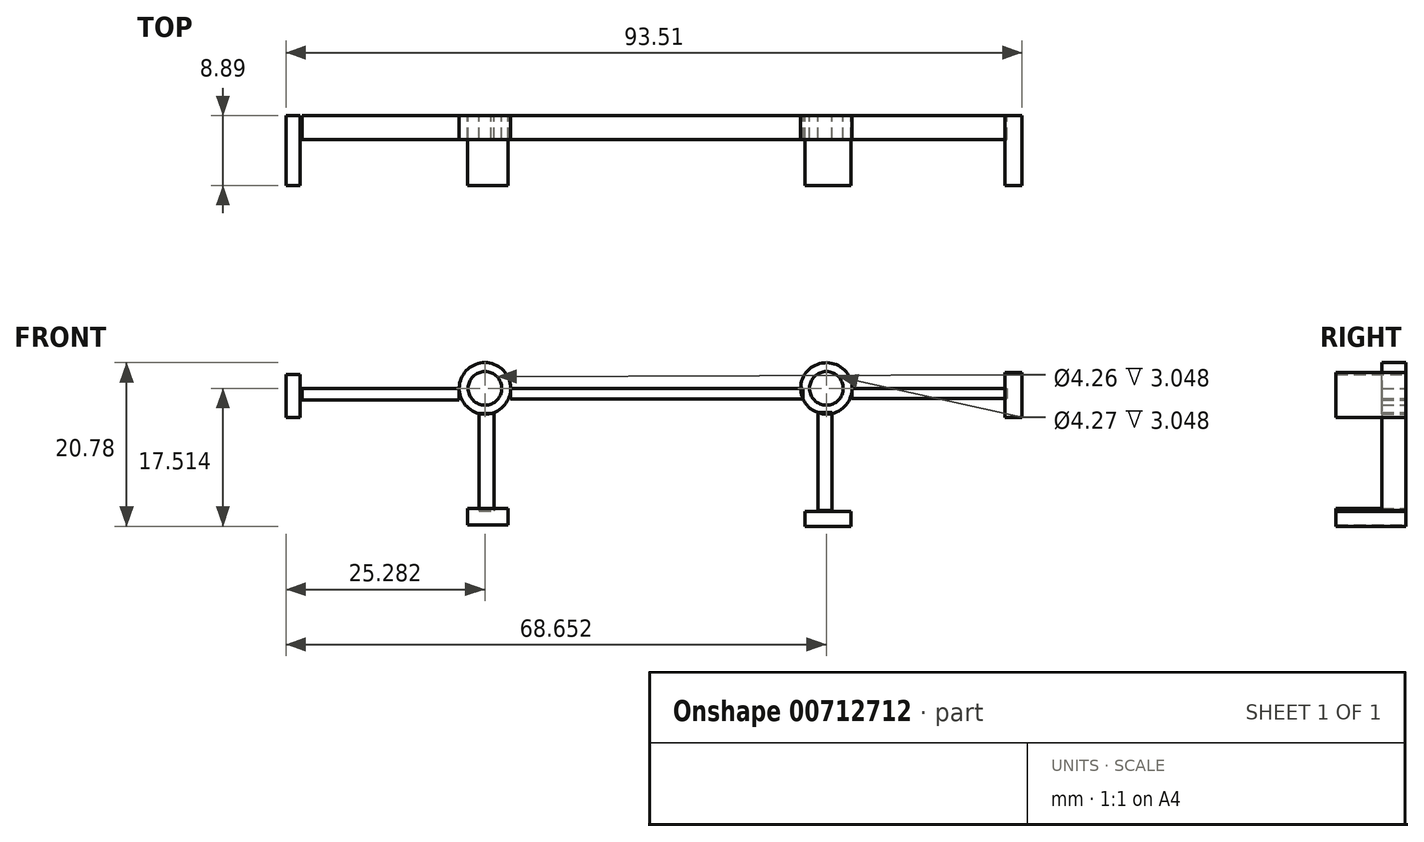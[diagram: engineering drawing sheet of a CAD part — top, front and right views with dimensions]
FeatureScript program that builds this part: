
annotation { "Feature Type Name" : "Feature", "Feature Type Description" : "" }
export const myFeature = defineFeature(function(context is Context, id is Id, definition is map)
    precondition{}
    {
        {
            var Q0;
            Q0=qCreatedBy(makeId("Front.planeOp"),FACE);
            var sketch = newSketch(context, id + "F0", { "sketchPlane" : qUnion([Q0])});
            skCircle(sketch, "E0", {"center": v(-24.54, 12.82) * mm, "radius": 3.27 * mm});
            skCircle(sketch, "E1", {"center": v(-24.54, 12.82) * mm, "radius": 2.13 * mm});
            skCircle(sketch, "E2", {"center": v(18.83, 12.82) * mm, "radius": 2.13 * mm});
            skCircle(sketch, "E3", {"center": v(18.83, 12.82) * mm, "radius": 3.26 * mm});
            skLineSegment(sketch, "E4.bottom", {"start": v(-21.27, 12.82) * mm, "end": v(15.87, 12.82) * mm});
            skLineSegment(sketch, "E4.top", {"start": v(-21.27, 11.46) * mm, "end": v(15.87, 11.46) * mm});
            skLineSegment(sketch, "E4.left", {"start": v(-21.27, 12.82) * mm, "end": v(-21.27, 11.46) * mm});
            skLineSegment(sketch, "E4.right", {"start": v(15.87, 12.82) * mm, "end": v(15.87, 11.46) * mm});
            skLineSegment(sketch, "E5.bottom", {"start": v(22.1, 12.82) * mm, "end": v(42.03, 12.82) * mm});
            skLineSegment(sketch, "E5.top", {"start": v(22.1, 11.55) * mm, "end": v(42.03, 11.55) * mm});
            skLineSegment(sketch, "E5.left", {"start": v(22.1, 12.82) * mm, "end": v(22.1, 11.55) * mm});
            skLineSegment(sketch, "E5.right", {"start": v(42.03, 12.82) * mm, "end": v(42.03, 11.55) * mm});
            skLineSegment(sketch, "E6.bottom", {"start": v(-27.8, 12.82) * mm, "end": v(-47.75, 12.82) * mm});
            skLineSegment(sketch, "E6.top", {"start": v(-27.8, 11.34) * mm, "end": v(-47.75, 11.34) * mm});
            skLineSegment(sketch, "E6.left", {"start": v(-27.8, 12.82) * mm, "end": v(-27.8, 11.34) * mm});
            skLineSegment(sketch, "E6.right", {"start": v(-47.75, 12.82) * mm, "end": v(-47.75, 11.34) * mm});
            skLineSegment(sketch, "E7.bottom", {"start": v(-24.54, 16.1) * mm, "end": v(-24.54, 16.1) * mm});
            skLineSegment(sketch, "E8.bottom", {"start": v(-25.29, 9.64) * mm, "end": v(-23.4, 9.64) * mm});
            skLineSegment(sketch, "E8.top", {"start": v(-25.29, -2.76) * mm, "end": v(-23.4, -2.76) * mm});
            skLineSegment(sketch, "E8.left", {"start": v(-25.29, 9.64) * mm, "end": v(-25.29, -2.76) * mm});
            skLineSegment(sketch, "E8.right", {"start": v(-23.4, 9.64) * mm, "end": v(-23.4, -2.76) * mm});
            skLineSegment(sketch, "E9.bottom", {"start": v(17.78, 9.74) * mm, "end": v(19.53, 9.74) * mm});
            skLineSegment(sketch, "E9.top", {"start": v(17.78, -2.66) * mm, "end": v(19.53, -2.66) * mm});
            skLineSegment(sketch, "E9.left", {"start": v(17.78, 9.74) * mm, "end": v(17.78, -2.66) * mm});
            skLineSegment(sketch, "E9.right", {"start": v(19.53, 9.74) * mm, "end": v(19.53, -2.66) * mm});
            skLineSegment(sketch, "E10.bottom", {"start": v(-48.17, 16.25) * mm, "end": v(-49.67, 16.25) * mm});
            skLineSegment(sketch, "E10.top", {"start": v(-48.17, 7.7) * mm, "end": v(-49.67, 7.7) * mm});
            skLineSegment(sketch, "E10.left", {"start": v(-48.17, 16.25) * mm, "end": v(-48.17, 7.7) * mm});
            skLineSegment(sketch, "E10.right", {"start": v(-49.67, 16.25) * mm, "end": v(-49.67, 7.7) * mm});
            skLineSegment(sketch, "E11.bottom", {"start": v(41.75, 16.9) * mm, "end": v(43.45, 16.9) * mm});
            skLineSegment(sketch, "E11.top", {"start": v(41.75, 7.28) * mm, "end": v(43.45, 7.28) * mm});
            skLineSegment(sketch, "E11.left", {"start": v(41.75, 16.9) * mm, "end": v(41.75, 7.28) * mm});
            skLineSegment(sketch, "E11.right", {"start": v(43.45, 16.9) * mm, "end": v(43.45, 7.28) * mm});
            skLineSegment(sketch, "E12.bottom", {"start": v(-28.31, -2.76) * mm, "end": v(-20.62, -2.76) * mm});
            skLineSegment(sketch, "E12.top", {"start": v(-28.31, -5.1) * mm, "end": v(-20.62, -5.1) * mm});
            skLineSegment(sketch, "E12.left", {"start": v(-28.31, -2.76) * mm, "end": v(-28.31, -5.1) * mm});
            skLineSegment(sketch, "E12.right", {"start": v(-20.62, -2.76) * mm, "end": v(-20.62, -5.1) * mm});
            skLineSegment(sketch, "E13.bottom", {"start": v(15.26, -2.66) * mm, "end": v(22.1, -2.66) * mm});
            skLineSegment(sketch, "E13.top", {"start": v(15.26, -5.1) * mm, "end": v(22.1, -5.1) * mm});
            skLineSegment(sketch, "E13.left", {"start": v(15.26, -2.66) * mm, "end": v(15.26, -5.1) * mm});
            skLineSegment(sketch, "E13.right", {"start": v(22.1, -2.66) * mm, "end": v(22.1, -5.1) * mm});
            skSolve(sketch);
        }
        {
            var Q0;
            {var subQ0=sQuery(id+"F0.wireOp",EDGE,"E5.left");Q0=makeQuery(id+"F0.imprint","IMPRINT",FACE,{"disambiguationData":[TD([[makeQuery(id+"F0.imprint","IMPRINT",EDGE,{"derivedFrom":subQ0}),1.0]])]});}
            var Q1;
            Q1=makeQuery(id+"F0.imprint","IMPRINT",FACE,{"disambiguationData":[TD([[makeQuery(id+"F0.imprint","IMPRINT",EDGE,{"derivedFrom":sQuery(id+"F0.wireOp",EDGE,"E2")}),-1.0]])]});
            var Q2;
            {var subQ0=sQuery(id+"F0.wireOp",EDGE,"E4.top");Q2=makeQuery(id+"F0.imprint","IMPRINT",FACE,{"disambiguationData":[TD([[makeQuery(id+"F0.imprint","IMPRINT",EDGE,{"derivedFrom":subQ0}),1.0]])]});}
            var Q3;
            Q3=makeQuery(id+"F0.imprint","IMPRINT",FACE,{"disambiguationData":[TD([[makeQuery(id+"F0.imprint","IMPRINT",EDGE,{"derivedFrom":sQuery(id+"F0.wireOp",EDGE,"E1")}),-1.0]])]});
            var Q4;
            Q4=makeQuery(id+"F0.imprint","IMPRINT",FACE,{"disambiguationData":[TD([[makeQuery(id+"F0.imprint","IMPRINT",EDGE,{"derivedFrom":sQuery(id+"F0.wireOp",EDGE,"E6.bottom")}),1.0]])]});
            var Q5;
            {var subQ1=sQuery(id+"F0.wireOp",EDGE,"E8.left");Q5=makeQuery(id+"F0.imprint","IMPRINT",FACE,{"disambiguationData":[TD([[makeQuery(id+"F0.imprint","IMPRINT",EDGE,{"derivedFrom":subQ1}),1.0]])]});}
            var Q6;
            {var subQ0=sQuery(id+"F0.wireOp",EDGE,"E9.left");Q6=makeQuery(id+"F0.imprint","IMPRINT",FACE,{"disambiguationData":[TD([[makeQuery(id+"F0.imprint","IMPRINT",EDGE,{"derivedFrom":subQ0}),1.0]])]});}
            extrude(context, id + "F1", {"entities" : qUnion([Q0, Q1, Q2, Q3, Q4, Q5, Q6]), "depth" : 3.05 * mm, "offsetDistance" : 25.4 * mm});
        }
        {
            var Q0;
            Q0=qCreatedBy(makeId("Front.planeOp"),FACE);
            var sketch = newSketch(context, id + "F2", { "sketchPlane" : qUnion([Q0])});
            skLineSegment(sketch, "E14.bottom", {"start": v(-48.02, 14.61) * mm, "end": v(-49.82, 14.61) * mm});
            skLineSegment(sketch, "E14.top", {"start": v(-48.02, 9.14) * mm, "end": v(-49.82, 9.14) * mm});
            skLineSegment(sketch, "E14.left", {"start": v(-48.02, 14.61) * mm, "end": v(-48.02, 9.14) * mm});
            skLineSegment(sketch, "E14.right", {"start": v(-49.82, 14.61) * mm, "end": v(-49.82, 9.14) * mm});
            skLineSegment(sketch, "E15.bottom", {"start": v(-26.74, -2.45) * mm, "end": v(-21.62, -2.45) * mm});
            skLineSegment(sketch, "E15.top", {"start": v(-26.74, -4.51) * mm, "end": v(-21.62, -4.51) * mm});
            skLineSegment(sketch, "E15.left", {"start": v(-26.74, -2.45) * mm, "end": v(-26.74, -4.51) * mm});
            skLineSegment(sketch, "E15.right", {"start": v(-21.62, -2.45) * mm, "end": v(-21.62, -4.51) * mm});
            skLineSegment(sketch, "E16.bottom", {"start": v(16.1, -2.8) * mm, "end": v(21.94, -2.8) * mm});
            skLineSegment(sketch, "E16.top", {"start": v(16.1, -4.7) * mm, "end": v(21.94, -4.7) * mm});
            skLineSegment(sketch, "E16.left", {"start": v(16.1, -2.8) * mm, "end": v(16.1, -4.7) * mm});
            skLineSegment(sketch, "E16.right", {"start": v(21.94, -2.8) * mm, "end": v(21.94, -4.7) * mm});
            skLineSegment(sketch, "E17.bottom", {"start": v(41.53, 14.86) * mm, "end": v(43.69, 14.86) * mm});
            skLineSegment(sketch, "E17.top", {"start": v(41.53, 9.14) * mm, "end": v(43.69, 9.14) * mm});
            skLineSegment(sketch, "E17.left", {"start": v(41.53, 14.86) * mm, "end": v(41.53, 9.14) * mm});
            skLineSegment(sketch, "E17.right", {"start": v(43.69, 14.86) * mm, "end": v(43.69, 9.14) * mm});
            skSolve(sketch);
        }
        {
            var Q0;
            Q0=makeQuery(id+"F2.imprint","IMPRINT",FACE,{"disambiguationData":[TD([[makeQuery(id+"F2.imprint","IMPRINT",EDGE,{"derivedFrom":sQuery(id+"F2.wireOp",EDGE,"E14.bottom")}),1.0]])]});
            var Q1;
            Q1=makeQuery(id+"F2.imprint","IMPRINT",FACE,{"disambiguationData":[TD([[makeQuery(id+"F2.imprint","IMPRINT",EDGE,{"derivedFrom":sQuery(id+"F2.wireOp",EDGE,"E15.bottom")}),-1.0]])]});
            var Q2;
            Q2=makeQuery(id+"F2.imprint","IMPRINT",FACE,{"disambiguationData":[TD([[makeQuery(id+"F2.imprint","IMPRINT",EDGE,{"derivedFrom":sQuery(id+"F2.wireOp",EDGE,"E16.bottom")}),-1.0]])]});
            var Q3;
            Q3=makeQuery(id+"F2.imprint","IMPRINT",FACE,{"disambiguationData":[TD([[makeQuery(id+"F2.imprint","IMPRINT",EDGE,{"derivedFrom":sQuery(id+"F2.wireOp",EDGE,"E17.bottom")}),-1.0]])]});
            extrude(context, id + "F3", {"entities" : qUnion([Q0, Q1, Q2, Q3]), "depth" : 8.9 * mm, "offsetDistance" : 25.4 * mm});
        }
    });
